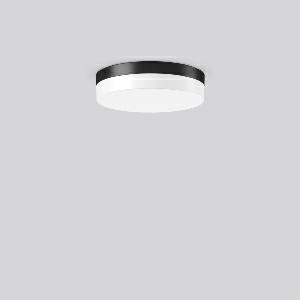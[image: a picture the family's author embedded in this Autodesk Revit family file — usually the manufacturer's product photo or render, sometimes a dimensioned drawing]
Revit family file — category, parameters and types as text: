
# Revit family: flat_slim_round_312629_0031_730_b5af
name_source: partatom
category: Lighting Fixtures
units: mm (PartAtom-declared; Revit-internal decimal feet)

## family parameters
Cut with Voids When Loaded = No
Host = Face
Light Source = No
Part Type = Normal
Room Calculation Point = No
Round Connector Dimension = Use Diameter
Shared = No

## types (1)
- MultiLumen 1 830 (1 x LED Modul 830, 1250 lm, 3000)
    Apparent Load = 13 VA
    CIE Flux Codes = 38 68 89 82 100
    Color Rendering = 80
    Color Temperature = 3000
    Default Elevation = 1800 mm
    Height = 75 mm
    Lamp = 1 x LED Modul 830
    Lamp Light Flux = 1250 lm
    Lamp count = 1
    Length = 300 mm
    Lifetime = 50000 h
    Luminous efficacy = 96 lm/W
    Manufacturer = RZB
    ModVariant = No
    Model = 312629.0031.730
    Mounting Place = Ceiling
    Mounting Type = Surface mounted
    Number of Poles = 1
    OnlyDefault = Yes
    Power Factor = 1
    Product Name = FLAT SLIM round
    Product group = Surface mounted ceiling and wall luminaires
    ProductGroupID = 305
    Protection Class = Protection class I
    Protection Degree = Degree of protection
    RLX_Detail_Level = 1
    RLX_Emergency_Light_Flux = 0 lm
    RLX_Emergency_Type = 0
    RLX_Emergency_Type_DB = No
    RlxData = <blob elided: 17589 chars, md5=8be36fa3>
    Socket = socket
    Standby Power = 0 W
    System Light Flux = 1250 lm
    System Power = 13 W
    Type Comments = MultiLumen 1 830
    Type Image = 312629.0031.jpg
    URL = http://relux.com
    VarID = multilumen_1_830
    Voltage = 0 V
    Weight = 0.00 kg
    Width = 0 mm  [stored 0 ft]

note: [stored X ft] marks values corroborated as IEEE doubles in the binary element streams (Revit-internal decimal feet)

## geometry (parser evidence)
native form markers: Blend x4, Sweep x14
no freeform markers — native parametric forms only
